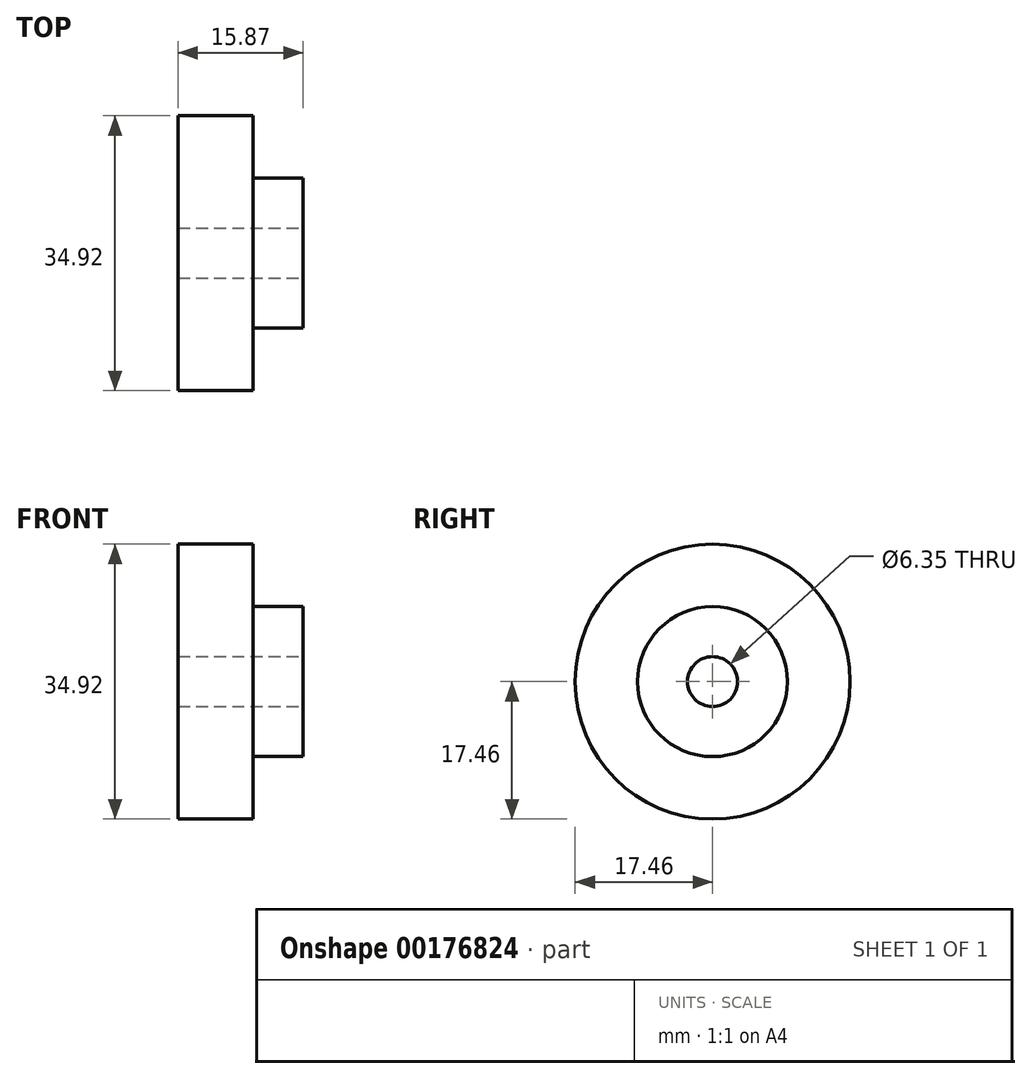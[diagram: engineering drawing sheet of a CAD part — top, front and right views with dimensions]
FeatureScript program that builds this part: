
annotation { "Feature Type Name" : "Feature", "Feature Type Description" : "" }
export const myFeature = defineFeature(function(context is Context, id is Id, definition is map)
    precondition{}
    {
        {
            var Q0;
            Q0=qCreatedBy(makeId("Front.planeOp"),FACE);
            var sketch = newSketch(context, id + "F0", { "sketchPlane" : qUnion([Q0])});
            skLineSegment(sketch, "E0", {"start": v(13.74, 3.18) * mm, "end": v(13.74, 9.53) * mm});
            skLineSegment(sketch, "E1", {"start": v(13.74, 9.53) * mm, "end": v(7.4, 9.53) * mm});
            skLineSegment(sketch, "E2", {"start": v(7.4, 9.53) * mm, "end": v(7.4, 17.46) * mm});
            skLineSegment(sketch, "E3", {"start": v(7.4, 17.46) * mm, "end": v(-2.13, 17.46) * mm});
            skLineSegment(sketch, "E4", {"start": v(-2.13, 17.46) * mm, "end": v(-2.13, 3.18) * mm});
            skLineSegment(sketch, "E5", {"start": v(-2.13, 3.18) * mm, "end": v(13.74, 3.18) * mm});
            skLineSegment(sketch, "E6", {"start": v(4.12, 0) * mm, "end": v(-4.41, 0) * mm, "construction": true});
            skSolve(sketch);
        }
        {
            var Q0;
            Q0=qSketchRegion(id+"F0",true);
            var Q1;
            Q1=sQuery(id+"F0.wireOp",EDGE,"E6");
            revolve(context, id + "F1", {"entities" : qUnion([Q0]), "axis" : qUnion([Q1]), "revolveType" : RevolveType.FULL});
        }
    });
